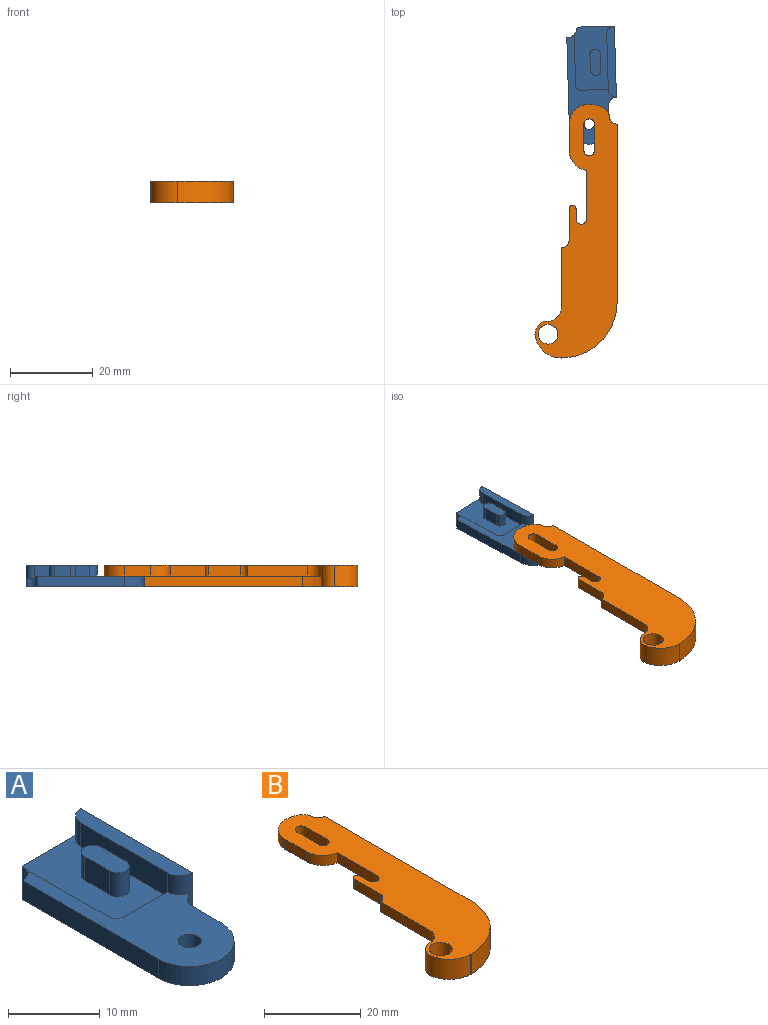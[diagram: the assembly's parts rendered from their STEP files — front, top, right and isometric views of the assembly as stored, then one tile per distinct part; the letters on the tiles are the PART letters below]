
ASSEMBLY  parts=2 mates=1
PART A: 23 faces, bbox 11.6x28.3x5.1 mm
  f0: plane 6.35x2.54mm, normal (0,0,1), area 14.7mm2, adj f1,f2,f21,f22
  f1: plane 3.81x3.18mm, normal (-1,0,0), area 12.1mm2, adj f0,f16,f21,f22
  f2: plane 3.81x3.18mm, normal (1,0,0), area 12.1mm2, adj f0,f16,f21,f22
  f3: plane 26.53x11.56mm, normal (0,0,1), area 136.3mm2, adj f7,f10,f12,f13,f14,f15,f17,f18
  f4: plane 9.02x1.91mm, normal (0,1,0), area 17.2mm2, adj f8,f9,f10,f16
  f5: plane 13.34x3.18mm, normal (-1,0,0), area 42.3mm2, adj f6,f11,f12,f14,f16
  f6: plane 17.15x1.91mm, normal (0,0,1), area 31.1mm2, adj f5,f8,f11,f12
  f7: plane 20.96x2.54mm, normal (-1,0,0), area 53.2mm2, adj f3,f9,f10,f19
  f8: plane 17.15x5.08mm, normal (1,0,0), area 87.1mm2, adj f4,f6,f9,f11,f12,f13
  f9: plane 28.32x11.56mm, normal (0,0,-1), area 286.7mm2, adj f4,f7,f8,f10,f13,f18,f19,f20
  f10: cylinder r=2.54mm len=2.54mm, axis (0,0,1), area 8.9mm2, adj f3,f4,f7,f9,f15,f16
  f11: cylinder r=1.91mm len=3.18mm, axis (0,0,-1), area 9.5mm2, adj f5,f6,f8,f16
  f12: cylinder r=1.91mm len=2.54mm, axis (0,0,1), area 7.6mm2, adj f3,f5,f6,f8
  f13: cylinder r=1.91mm len=2.54mm, axis (0,0,1), area 7.6mm2, adj f3,f8,f9,f18
  f14: plane 6.59x0.64mm, normal (0,1,0), area 4.2mm2, adj f3,f5,f16,f17
  f15: plane 12.17x0.64mm, normal (1,0,0), area 7.7mm2, adj f3,f10,f16,f17
  f16: plane 15.24x9.76mm, normal (0,0,1), area 104.5mm2, adj f1,f2,f4,f5,f10,f11,f14,f15
  f17: cylinder r=1.27mm len=1.27mm, axis (0,0,1), area 1.3mm2, adj f3,f14,f15,f16
  f18: plane 4.45x2.54mm, normal (1,0,0), area 11.3mm2, adj f3,f9,f13,f19
  f19: cylinder r=4.83mm len=9.65mm, axis (0,0,1), area 38.5mm2, adj f3,f7,f9,f18
  f20: cylinder r=1.27mm len=2.54mm, axis (0,0,1), area 20.3mm2, adj f3,f9
  f21: cylinder r=1.27mm len=3.18mm, axis (0,0,-1), area 12.7mm2, adj f0,f1,f2,f16
  f22: cylinder r=1.27mm len=3.18mm, axis (0,0,1), area 12.7mm2, adj f0,f1,f2,f16
PART B: 32 faces, bbox 19.8x61.2x5.1 mm
  f0: plane 59.18x16.64mm, normal (0,0,-1), area 516.3mm2, adj f1,f3,f4,f6,f7,f8,f9,f10
  f1: cylinder r=4.83mm len=4.83mm, axis (0,0,-1), area 19.3mm2, adj f0,f4,f5,f22
  f2: plane 56.39x19.81mm, normal (0,0,-1), area 145mm2, adj f10,f11,f19,f20,f21,f24,f25,f26
  f3: cylinder r=4.83mm len=4.78mm, axis (0,0,-1), area 17.6mm2, adj f0,f4,f5,f12
  f4: plane 6.35x2.54mm, normal (-1,0,0), area 16.1mm2, adj f0,f1,f3,f5
  f5: plane 61.21x19.81mm, normal (0,0,1), area 661.2mm2, adj f1,f3,f4,f6,f7,f8,f9,f11
  f6: cylinder r=1.27mm len=2.54mm, axis (0,0,1), area 10.1mm2, adj f0,f5,f7,f9
  f7: plane 6.35x2.54mm, normal (-1,0,0), area 16.1mm2, adj f0,f5,f6,f8
  f8: cylinder r=1.27mm len=2.54mm, axis (0,0,1), area 10.1mm2, adj f0,f5,f7,f9
  f9: plane 6.35x2.54mm, normal (1,0,0), area 16.1mm2, adj f0,f5,f6,f8
  f10: plane 41.02x2.54mm, normal (-1,0,0), area 104.2mm2, adj f0,f2,f20,f21
  f11: plane 42.93x5.08mm, normal (1,0,0), area 218.1mm2, adj f2,f5,f19,f21,f23
  f12: plane 11.73x2.54mm, normal (-1,0,0), area 29.8mm2, adj f0,f3,f5,f15
  f13: cylinder r=0.83mm len=2.54mm, axis (0,0,1), area 6.6mm2, adj f0,f5,f14,f16
  f14: plane 2.54x2.54mm, normal (1,0,0), area 6.5mm2, adj f0,f5,f13,f15
  f15: cylinder r=1.27mm len=2.54mm, axis (0,0,1), area 10.1mm2, adj f0,f5,f12,f14
  f16: plane 7.62x2.54mm, normal (-1,0,0), area 19.4mm2, adj f0,f5,f13,f17
  f17: cylinder r=1.91mm len=2.54mm, axis (0,0,1), area 7.6mm2, adj f0,f5,f16,f18
  f18: plane 14.48x2.54mm, normal (-1,0,0), area 36.8mm2, adj f0,f5,f17,f30
  f19: cylinder r=13.46mm len=13.46mm, axis (0,0,1), area 107.4mm2, adj f2,f5,f11,f24
  f20: cylinder r=11.56mm len=11.41mm, axis (0,0,1), area 41.4mm2, adj f0,f2,f10,f31
  f21: cylinder r=1.91mm len=2.54mm, axis (0,0,-1), area 7.6mm2, adj f0,f2,f10,f11
  f22: extruded ~4.83x2.92mm, area 15.7mm2, adj f0,f1,f5,f23
  f23: cylinder r=1.91mm len=2.54mm, axis (0,0,1), area 7.6mm2, adj f0,f5,f11,f22
  f24: plane 5.08x0.03mm, normal (0,-1,0), area 0.2mm2, adj f2,f5,f19,f28
  f25: plane 2.54x2.1mm, normal (1,0,0), area 5.3mm2, adj f0,f2,f29,f31
  f26: cylinder r=2.38mm len=5.08mm, axis (0,0,-1), area 76mm2, adj f2,f5
  f27: cylinder r=3.17mm len=5.08mm, axis (0,0,-1), area 25.3mm2, adj f2,f5,f28,f29,f30
  f28: cylinder r=6.35mm len=6.32mm, axis (0,0,-1), area 47.4mm2, adj f2,f5,f24,f27
  f29: cylinder r=3.17mm len=3.18mm, axis (0,0,-1), area 12.7mm2, adj f0,f2,f25,f27
  f30: cylinder r=3.17mm len=3.18mm, axis (0,0,1), area 12.7mm2, adj f0,f5,f18,f27
  f31: cylinder r=1.59mm len=2.54mm, axis (0,0,1), area 7mm2, adj f0,f2,f20,f25
PLACE A rot(axis=(0,0,1),1.6deg) t=(-14.89,2.55,-13.36)mm
PLACE B t=(-15.47,-11.45,-10.82)mm
MATE planar A.f3 <-> B.f0  axis (0,0,1) through (-14.14,-3.14,-10.82)mm
